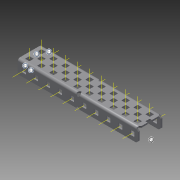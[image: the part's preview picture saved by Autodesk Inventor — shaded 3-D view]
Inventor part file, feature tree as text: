
AUTODESK INVENTOR PART (.ipt)
format: ipt  version: 2015 (Build 190159000, 159)  size: 2,007,040 bytes
history: native  units: in
note: dims shown in document units (in); Inventor stores cm internally (conversion verified against a paired STEP export)
features: other x57, pattern_linear x3, sheet_metal_op x1, extrude x1, imported_body x1, sketch x1
ambient origin geometry x8: Origin, YZ Plane, XZ Plane, XY Plane, X Axis, Y Axis, Z Axis, Center Point
bodies: Body1 (feature_tree)
feature tree (64):
  other  "C-Channel 2 x 10 (aluminum)"
  sheet_metal_op  "Fold1"
  other  "C-Channel"
  extrude  "length cut"  Depth=0.5in
  other  "top axis"
  other  "inner axis"
  other  "front axis"
  other  "back axis"
  pattern_linear  "top axes"  Spacing1=0.5in  [1 undecoded]
  pattern_linear  "inner axes"  Spacing1=0.5in  [1 undecoded]
  pattern_linear  "horiz axes"  Spacing1=-5.0in  [1 undecoded]
  other  "right plane"
  imported_body  "Base1"
  sketch  "Sketch1"  dims[d1=0.0in d4=0.5in d5=0.7874in d7=0.5in d10=0.5in d13=0.5in d14=-5.0in d15=0.0in d16=0.0in d17=0.0in d18=0.0in d19=0.0in]
  other  "Work Point1"
  other  "Work Point2"
  other  "Work Point3"
  other  "Work Point4"
  other  "Work Axis5"
  other  "Work Axis6"
  other  "Work Axis7"
  other  "Work Axis8"
  other  "Work Axis11"
  other  "Work Axis12"
  other  "Work Axis13"
  other  "Work Axis14"
  other  "Work Axis15"
  other  "Work Axis18"
  other  "Work Axis19"
  other  "Work Axis20"
  other  "Work Axis23"
  other  "Work Axis24"
  other  "Work Axis25"
  other  "Work Axis26"
  other  "Work Axis30"
  other  "Work Axis31"
  other  "Work Axis32"
  other  "Work Axis33"
  other  "left plane"
  other  "Work Axis137"
  other  "Work Axis138"
  other  "Work Axis139"
  other  "Work Axis140"
  other  "Work Axis141"
  other  "Work Axis142"
  other  "Work Axis143"
  other  "Work Axis144"
  other  "Work Axis145"
  other  "Work Axis146"
  other  "Work Axis147"
  other  "Work Axis148"
  other  "Work Axis149"
  other  "Work Axis150"
  other  "Work Axis151"
  other  "Work Axis152"
  other  "Work Axis153"
  other  "Work Axis154"
  other  "Work Axis155"
  other  "Work Axis156"
  other  "Work Axis157"
  other  "Work Axis158"
  other  "Work Axis159"
  other  "Work Axis160"
  other  "Work Axis161"
note: 3 required parameter values undecoded (feature->parameter linkage not recoverable at this tier; creation-order binding heuristic only, values carry confidence <= 0.55)
